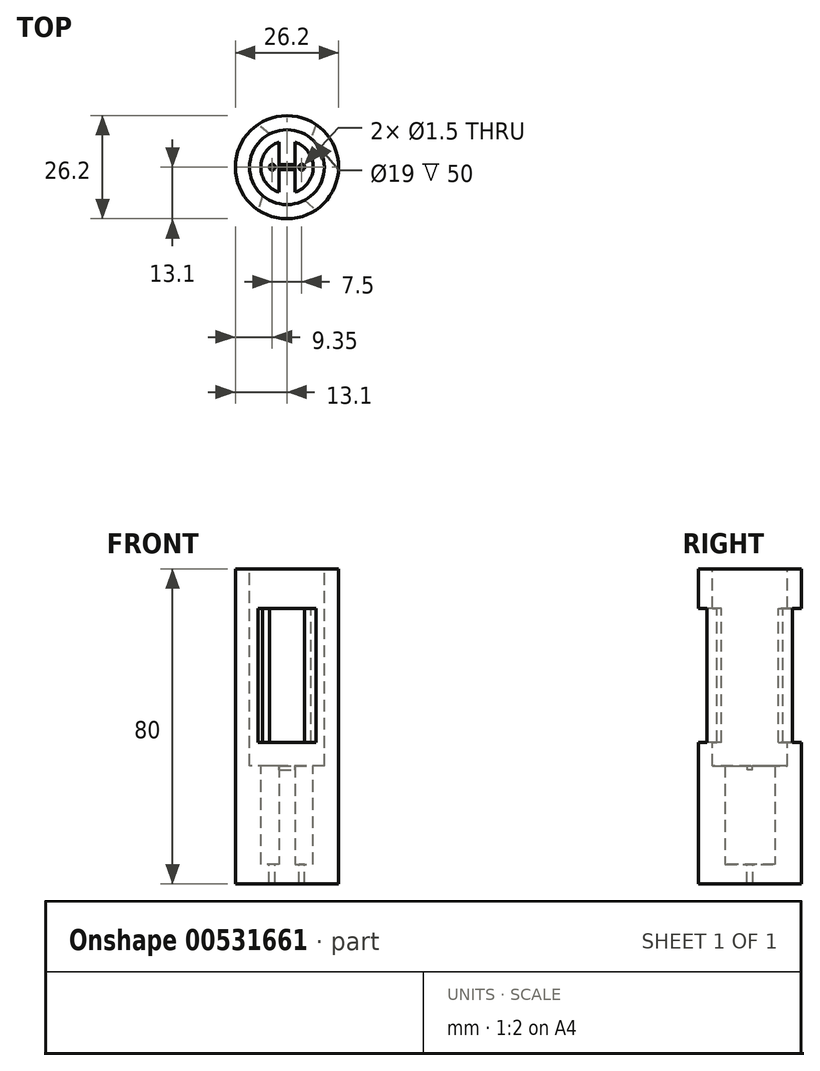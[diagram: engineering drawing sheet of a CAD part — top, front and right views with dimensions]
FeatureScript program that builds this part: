
annotation { "Feature Type Name" : "Feature", "Feature Type Description" : "" }
export const myFeature = defineFeature(function(context is Context, id is Id, definition is map)
    precondition{}
    {
        {
            var Q0;
            Q0=qCreatedBy(makeId("Top.planeOp"),FACE);
            var sketch = newSketch(context, id + "F0", { "sketchPlane" : qUnion([Q0])});
            skCircle(sketch, "E0", {"center": v(0, 0) * mm, "radius": 13.1 * mm});
            skSolve(sketch);
        }
        {
            var Q0;
            Q0=makeQuery(id+"F0.imprint","IMPRINT",FACE,{"disambiguationData":[TD([[makeQuery(id+"F0.imprint","IMPRINT",EDGE,{"derivedFrom":sQuery(id+"F0.wireOp",EDGE,"E0")}),1.0]])]});
            extrude(context, id + "F1", {"entities" : qUnion([Q0]), "depth" : 80 * mm, "offsetDistance" : 25 * mm});
        }
        {
            var Q0;
            Q0=makeQuery(id+"F1.opExtrude","CAP_FACE",FACE,{"disambiguationData":[OSD([sQuery(id+"F0.wireOp",EDGE,"E0")])],"isStart":false});
            var sketch = newSketch(context, id + "F2", { "sketchPlane" : qUnion([Q0])});
            skCircle(sketch, "E1", {"center": v(0, 0) * mm, "radius": 9.5 * mm});
            skSolve(sketch);
        }
        {
            var Q0;
            Q0=makeQuery(id+"F2.imprint","IMPRINT",FACE,{"disambiguationData":[TD([[makeQuery(id+"F2.imprint","IMPRINT",EDGE,{"derivedFrom":sQuery(id+"F2.wireOp",EDGE,"E1")}),1.0]])]});
            var Q1;
            Q1=sQuery(id+"F2.wireOp",EDGE,"E1");
            extrude(context, id + "F3", {"entities" : qUnion([Q0]), "operationType" : NewBodyOperationType.REMOVE, "surfaceEntities" : qUnion([Q1]), "oppositeDirection" : true, "depth" : 50 * mm, "offsetDistance" : 25 * mm});
        }
        {
            var Q0;
            Q0=makeQuery(id+"F3.boolean.opBoolean","COPY",FACE,{"derivedFrom":makeQuery(id+"F3.opExtrude","CAP_FACE",FACE,{"disambiguationData":[OSD([sQuery(id+"F2.wireOp",EDGE,"E1")])],"isStart":false})});
            var sketch = newSketch(context, id + "F4", { "sketchPlane" : qUnion([Q0])});
            skCircle(sketch, "E2", {"center": v(0, 0) * mm, "radius": 6.65 * mm});
            skSolve(sketch);
        }
        {
            var Q0;
            Q0=qSketchRegion(id+"F4",true);
            extrude(context, id + "F5", {"entities" : qUnion([Q0]), "operationType" : NewBodyOperationType.REMOVE, "oppositeDirection" : true, "depth" : 25 * mm, "offsetDistance" : 25 * mm});
        }
        {
            var Q0;
            Q0=makeQuery(id+"F5.boolean.opBoolean","COPY",FACE,{"derivedFrom":makeQuery(id+"F5.opExtrude","CAP_FACE",FACE,{"disambiguationData":[OSD([sQuery(id+"F4.wireOp",EDGE,"E2")])],"isStart":false})});
            var sketch = newSketch(context, id + "F6", { "sketchPlane" : qUnion([Q0])});
            skLineSegment(sketch, "E3", {"start": v(-2, 6.34) * mm, "end": v(-2, -6.34) * mm});
            skLineSegment(sketch, "E4", {"start": v(2, -6.34) * mm, "end": v(2, 6.34) * mm});
            skSolve(sketch);
        }
        {
            var Q0;
            {var subQ0=sQuery(id+"F6.wireOp",EDGE,"E3");Q0=makeQuery(id+"F6.imprint","IMPRINT",FACE,{"disambiguationData":[TD([[makeQuery(id+"F6.imprint","IMPRINT",EDGE,{"derivedFrom":subQ0}),1.0]])]});}
            extrude(context, id + "F7", {"entities" : qUnion([Q0]), "operationType" : NewBodyOperationType.ADD, "depth" : 25 * mm, "offsetDistance" : 25 * mm});
        }
        {
            var Q0;
            {var subQ0=sQuery(id+"F4.wireOp",EDGE,"E2");Q0=makeQuery(id+"F7.boolean.opBoolean","SPLIT",FACE,{"disambiguationData":[TD([makeQuery(id+"F7.opExtrude","SWEPT_FACE",FACE,{"disambiguationData":[OSD([sQuery(id+"F6.wireOp",EDGE,"E3")])]})])],"derivedFrom":makeQuery(id+"F5.boolean.opBoolean","COPY",FACE,{"derivedFrom":makeQuery(id+"F5.opExtrude","CAP_FACE",FACE,{"disambiguationData":[OSD([subQ0])],"isStart":false})})});}
            var sketch = newSketch(context, id + "F8", { "sketchPlane" : qUnion([Q0])});
            skCircle(sketch, "E5", {"center": v(-3.75, 0) * mm, "radius": 0.75 * mm});
            skCircle(sketch, "E6", {"center": v(3.75, 0) * mm, "radius": 0.75 * mm});
            skSolve(sketch);
        }
        {
            var Q0;
            Q0=qSketchRegion(id+"F8",true);
            extrude(context, id + "F9", {"entities" : qUnion([Q0]), "operationType" : NewBodyOperationType.REMOVE, "oppositeDirection" : true, "depth" : 5 * mm, "offsetDistance" : 25 * mm});
        }
        {
            var Q0;
            Q0=makeQuery(id+"F7.opExtrude","CAP_FACE",FACE,{"disambiguationData":[OSD([sQuery(id+"F4.wireOp",EDGE,"E2"),sQuery(id+"F6.wireOp",EDGE,"E3"),sQuery(id+"F6.wireOp",EDGE,"E4")])],"isStart":false});
            var sketch = newSketch(context, id + "F10", { "sketchPlane" : qUnion([Q0])});
            skLineSegment(sketch, "E7", {"start": v(-2, 0.6) * mm, "end": v(2, 0.6) * mm});
            skLineSegment(sketch, "E8", {"start": v(-2, -0.6) * mm, "end": v(2, -0.6) * mm});
            skSolve(sketch);
        }
        {
            var Q0;
            {var subQ0=sQuery(id+"F10.wireOp",EDGE,"E7");Q0=makeQuery(id+"F10.imprint","IMPRINT",FACE,{"disambiguationData":[TD([[makeQuery(id+"F10.imprint","IMPRINT",EDGE,{"derivedFrom":subQ0}),-1.0]])]});}
            extrude(context, id + "F11", {"entities" : qUnion([Q0]), "operationType" : NewBodyOperationType.REMOVE, "oppositeDirection" : true, "depth" : 1 * mm, "offsetDistance" : 25 * mm});
        }
        {
            var Q0;
            Q0=makeQuery(id+"F1.opExtrude","CAP_FACE",FACE,{"disambiguationData":[OSD([sQuery(id+"F0.wireOp",EDGE,"E0")])],"isStart":false});
            var sketch = newSketch(context, id + "F12", { "sketchPlane" : qUnion([Q0])});
            skLineSegment(sketch, "E9", {"start": v(-4.43, 8.4) * mm, "end": v(-7.34, 10.85) * mm});
            skLineSegment(sketch, "E10", {"start": v(7.34, 10.85) * mm, "end": v(6.15, 7.24) * mm});
            skLineSegment(sketch, "E11", {"start": v(4.43, -8.4) * mm, "end": v(7.34, -10.85) * mm});
            skLineSegment(sketch, "E12", {"start": v(-6.15, -7.24) * mm, "end": v(-7.34, -10.85) * mm});
            skSolve(sketch);
        }
        {
            var Q0;
            {var subQ0=sQuery(id+"F12.wireOp",EDGE,"E9");Q0=makeQuery(id+"F12.imprint","IMPRINT",FACE,{"disambiguationData":[TD([[makeQuery(id+"F12.imprint","IMPRINT",EDGE,{"derivedFrom":subQ0}),-1.0]])]});}
            extrude(context, id + "F13", {"entities" : qUnion([Q0]), "operationType" : NewBodyOperationType.REMOVE, "oppositeDirection" : true, "depth" : 44 * mm, "offsetDistance" : 25 * mm});
        }
        {
            var Q0;
            {var subQ0=sQuery(id+"F12.wireOp",EDGE,"E11");Q0=makeQuery(id+"F12.imprint","IMPRINT",FACE,{"disambiguationData":[TD([[makeQuery(id+"F12.imprint","IMPRINT",EDGE,{"derivedFrom":subQ0}),-1.0]])]});}
            extrude(context, id + "F14", {"entities" : qUnion([Q0]), "operationType" : NewBodyOperationType.REMOVE, "oppositeDirection" : true, "depth" : 44 * mm});
        }
        {
            var Q0;
            {var subQ0=sQuery(id+"F12.wireOp",EDGE,"E11");Q0=makeQuery(id+"F12.imprint","IMPRINT",FACE,{"disambiguationData":[TD([[makeQuery(id+"F12.imprint","IMPRINT",EDGE,{"derivedFrom":subQ0}),-1.0]])]});}
            extrude(context, id + "F15", {"entities" : qUnion([Q0]), "operationType" : NewBodyOperationType.ADD, "oppositeDirection" : true, "depth" : 10 * mm});
        }
        {
            var Q0;
            {var subQ0=sQuery(id+"F12.wireOp",EDGE,"E9");Q0=makeQuery(id+"F12.imprint","IMPRINT",FACE,{"disambiguationData":[TD([[makeQuery(id+"F12.imprint","IMPRINT",EDGE,{"derivedFrom":subQ0}),-1.0]])]});}
            extrude(context, id + "F16", {"entities" : qUnion([Q0]), "operationType" : NewBodyOperationType.ADD, "oppositeDirection" : true, "depth" : 10 * mm});
        }
    });
